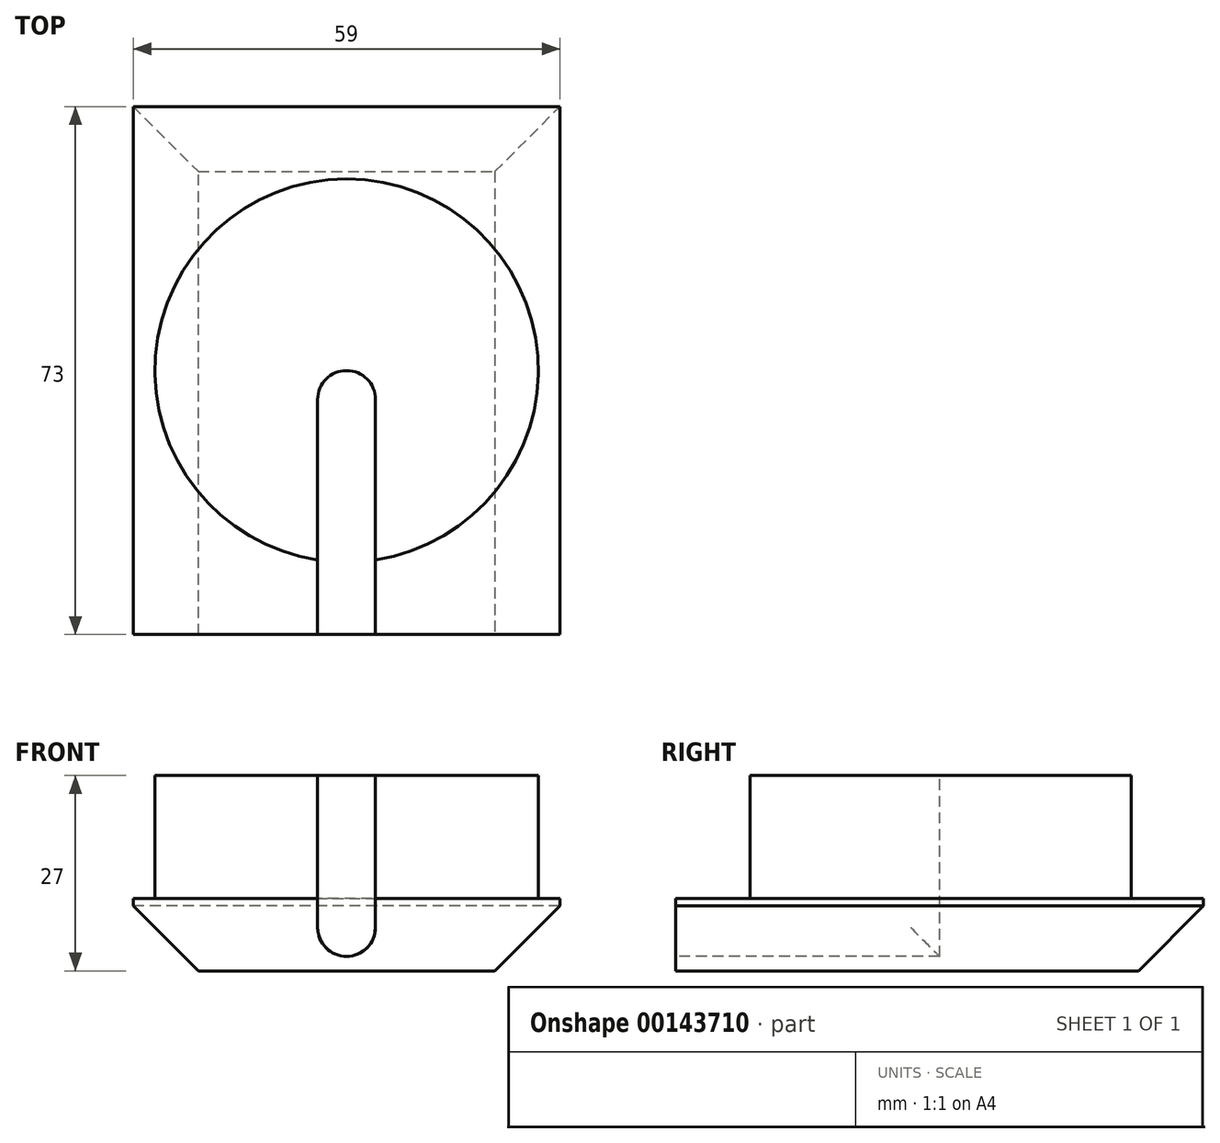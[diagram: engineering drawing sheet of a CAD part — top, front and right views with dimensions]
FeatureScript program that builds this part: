
annotation { "Feature Type Name" : "Feature", "Feature Type Description" : "" }
export const myFeature = defineFeature(function(context is Context, id is Id, definition is map)
    precondition{}
    {
        {
            var Q0;
            Q0=qCreatedBy(makeId("Top.planeOp"),FACE);
            var sketch = newSketch(context, id + "F0", { "sketchPlane" : qUnion([Q0])});
            skCircle(sketch, "E0", {"center": v(0, 0) * mm, "radius": 26.5 * mm});
            skLineSegment(sketch, "E1.bottom", {"start": v(0, 0) * mm, "end": v(0, 0) * mm});
            skLineSegment(sketch, "E2.bottom", {"start": v(-29.5, 36.5) * mm, "end": v(29.5, 36.5) * mm});
            skLineSegment(sketch, "E2.top", {"start": v(-29.5, -36.5) * mm, "end": v(29.5, -36.5) * mm});
            skLineSegment(sketch, "E2.left", {"start": v(-29.5, 36.5) * mm, "end": v(-29.5, -36.5) * mm});
            skLineSegment(sketch, "E2.right", {"start": v(29.5, 36.5) * mm, "end": v(29.5, -36.5) * mm});
            skSolve(sketch);
        }
        {
            var Q0;
            Q0=makeQuery(id+"F0.imprint","IMPRINT",FACE,{"disambiguationData":[TD([[makeQuery(id+"F0.imprint","IMPRINT",EDGE,{"derivedFrom":sQuery(id+"F0.wireOp",EDGE,"E0")}),1.0]])]});
            extrude(context, id + "F1", {"entities" : qUnion([Q0]), "depth" : 27 * mm});
        }
        {
            var Q0;
            Q0=makeQuery(id+"F0.imprint","IMPRINT",FACE,{"disambiguationData":[TD([[makeQuery(id+"F0.imprint","IMPRINT",EDGE,{"derivedFrom":sQuery(id+"F0.wireOp",EDGE,"E0")}),-1.0]])]});
            extrude(context, id + "F2", {"entities" : qUnion([Q0]), "operationType" : NewBodyOperationType.ADD, "depth" : 10 * mm});
        }
        {
            var Q0;
            Q0=makeQuery(id+"F2.opExtrude","SWEPT_FACE",FACE,{"disambiguationData":[OSD([sQuery(id+"F0.wireOp",EDGE,"E2.top")])]});
            var sketch = newSketch(context, id + "F3", { "sketchPlane" : qUnion([Q0])});
            skLineSegment(sketch, "E3", {"start": v(-4, 10) * mm, "end": v(-4, 6) * mm});
            skLineSegment(sketch, "E4.MirrorCS", {"start": v(4, 10) * mm, "end": v(4, 6) * mm});
            skArc(sketch, "E5", {"start": v(-4, 6) * mm, "mid": v(0, 2) * mm, "end": v(4, 6) * mm});
            skSolve(sketch);
        }
        {
            var Q0;
            {var subQ0=sQuery(id+"F3.wireOp",EDGE,"E3");Q0=makeQuery(id+"F3.imprint","IMPRINT",FACE,{"disambiguationData":[TD([[makeQuery(id+"F3.imprint","IMPRINT",EDGE,{"derivedFrom":subQ0}),1.0]])]});}
            extrude(context, id + "F4", {"entities" : qUnion([Q0]), "operationType" : NewBodyOperationType.REMOVE, "oppositeDirection" : true, "depth" : 10 * mm});
        }
        {
            var Q0;
            Q0=makeQuery(id+"F1.opExtrude","CAP_FACE",FACE,{"disambiguationData":[OSD([sQuery(id+"F0.wireOp",EDGE,"E0")])],"isStart":false});
            var sketch = newSketch(context, id + "F5", { "sketchPlane" : qUnion([Q0])});
            skLineSegment(sketch, "E6", {"start": v(-4, 0) * mm, "end": v(-4, -27) * mm});
            skLineSegment(sketch, "E7.MirrorCS", {"start": v(4, 0) * mm, "end": v(4, -27) * mm});
            skArc(sketch, "E8", {"start": v(4, -4) * mm, "mid": v(0, 0) * mm, "end": v(-4, -4) * mm});
            skLineSegment(sketch, "E9", {"start": v(-4, -27) * mm, "end": v(4, -27) * mm});
            skSolve(sketch);
        }
        {
            var Q0;
            {var subQ0=sQuery(id+"F5.wireOp",EDGE,"E9");Q0=makeQuery(id+"F5.imprint","IMPRINT",FACE,{"disambiguationData":[TD([[makeQuery(id+"F5.imprint","IMPRINT",EDGE,{"derivedFrom":subQ0}),1.0]])]});}
            var Q1;
            {var subQ0=sQuery(id+"F5.wireOp",EDGE,"E8");Q1=makeQuery(id+"F5.imprint","IMPRINT",FACE,{"disambiguationData":[TD([[makeQuery(id+"F5.imprint","IMPRINT",EDGE,{"derivedFrom":subQ0}),1.0]])]});}
            extrude(context, id + "F6", {"entities" : qUnion([Q0, Q1]), "operationType" : NewBodyOperationType.REMOVE, "oppositeDirection" : true, "depth" : 25 * mm});
        }
        {
            var Q0;
            Q0=makeQuery(id+"F6.boolean.opBoolean","COPY",FACE,{"disambiguationData":[OD(0.0)],"derivedFrom":makeQuery(id+"F6.opExtrude","SWEPT_FACE",FACE,{"disambiguationData":[OSD([sQuery(id+"F5.wireOp",EDGE,"E9")])]})});
            var Q1;
            Q1=makeQuery(id+"F6.boolean.opBoolean","COPY",FACE,{"disambiguationData":[OD(1.0)],"derivedFrom":makeQuery(id+"F6.opExtrude","SWEPT_FACE",FACE,{"disambiguationData":[OSD([sQuery(id+"F5.wireOp",EDGE,"E9")])]})});
            extrude(context, id + "F7", {"entities" : qUnion([Q0, Q1]), "operationType" : NewBodyOperationType.ADD, "depth" : 30 * mm});
        }
        {
            var Q0;
            Q0=makeQuery(id+"F2.opExtrude","CAP_EDGE",EDGE,{"disambiguationData":[OSD([sQuery(id+"F0.wireOp",EDGE,"E2.bottom")])],"isStart":true});
            var Q1;
            Q1=makeQuery(id+"F2.opExtrude","CAP_EDGE",EDGE,{"disambiguationData":[OSD([sQuery(id+"F0.wireOp",EDGE,"E2.left")])],"isStart":true});
            var Q2;
            Q2=makeQuery(id+"F2.opExtrude","CAP_EDGE",EDGE,{"disambiguationData":[OSD([sQuery(id+"F0.wireOp",EDGE,"E2.right")])],"isStart":true});
            chamfer(context, id + "F8", {"entities" : qUnion([Q0, Q1, Q2]), "width" : 9 * mm, "tangentPropagation" : true});
        }
    });
